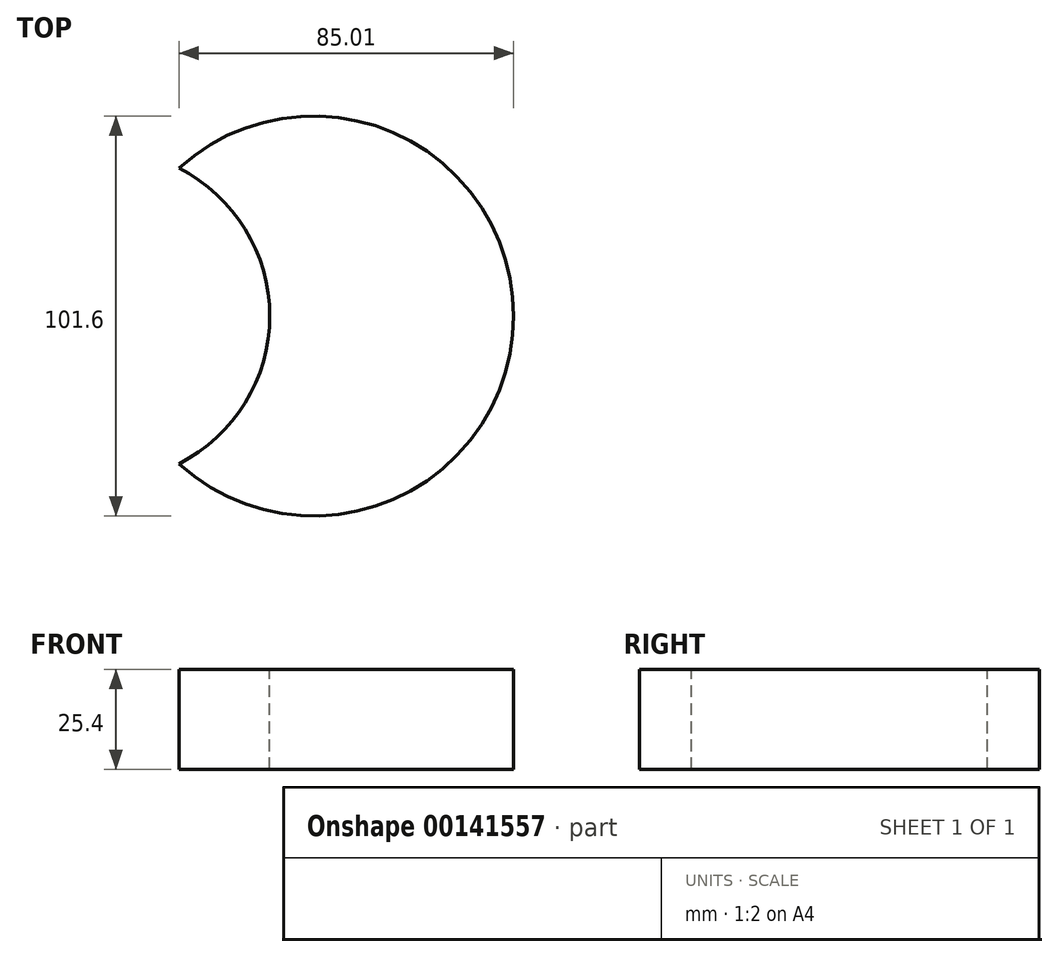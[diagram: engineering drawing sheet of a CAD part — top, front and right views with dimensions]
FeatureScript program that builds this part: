
annotation { "Feature Type Name" : "Feature", "Feature Type Description" : "" }
export const myFeature = defineFeature(function(context is Context, id is Id, definition is map)
    precondition{}
    {
        {
            var Q0;
            Q0=qCreatedBy(makeId("Top.planeOp"),FACE);
            var sketch = newSketch(context, id + "F0", { "sketchPlane" : qUnion([Q0])});
            skCircle(sketch, "E0", {"center": v(0, 0) * mm, "radius": 50.8 * mm});
            skSolve(sketch);
        }
        {
            var Q0;
            Q0=makeQuery(id+"F0.imprint","IMPRINT",FACE,{"disambiguationData":[TD([[makeQuery(id+"F0.imprint","IMPRINT",EDGE,{"derivedFrom":sQuery(id+"F0.wireOp",EDGE,"E0")}),1.0]])]});
            extrude(context, id + "F1", {"entities" : qUnion([Q0]), "depth" : 25.4 * mm});
        }
        {
            var Q0;
            Q0=makeQuery(id+"F1.opExtrude","CAP_FACE",FACE,{"disambiguationData":[OSD([sQuery(id+"F0.wireOp",EDGE,"E0")])],"isStart":false});
            var sketch = newSketch(context, id + "F2", { "sketchPlane" : qUnion([Q0])});
            skCircle(sketch, "E1", {"center": v(-53.22, 0) * mm, "radius": 42.1 * mm});
            skSolve(sketch);
        }
        {
            var Q0;
            {var subQ0=sQuery(id+"F2.wireOp",EDGE,"E1");var subQ1=makeQuery(id+"F1.opExtrude","CAP_EDGE",EDGE,{"disambiguationData":[OSD([sQuery(id+"F0.wireOp",EDGE,"E0")])],"isStart":false});var subQ2=makeQuery(id+"F2.imprint","INTERSECT",VERTEX,{"disambiguationData":[OD(0.0)],"derivedFrom":[subQ1,subQ0]});Q0=makeQuery(id+"F2.imprint","IMPRINT",FACE,{"disambiguationData":[TD([[makeQuery(id+"F2.imprint","IMPRINT",EDGE,{"disambiguationData":[TD([[subQ2,1.0]])],"derivedFrom":subQ0}),1.0]])]});}
            var Q1;
            {var subQ0=sQuery(id+"F2.wireOp",EDGE,"E1");var subQ1=makeQuery(id+"F1.opExtrude","CAP_EDGE",EDGE,{"disambiguationData":[OSD([sQuery(id+"F0.wireOp",EDGE,"E0")])],"isStart":false});var subQ2=makeQuery(id+"F2.imprint","INTERSECT",VERTEX,{"disambiguationData":[OD(0.0)],"derivedFrom":[subQ1,subQ0]});Q1=makeQuery(id+"F2.imprint","IMPRINT",FACE,{"disambiguationData":[TD([[makeQuery(id+"F2.imprint","IMPRINT",EDGE,{"disambiguationData":[TD([[subQ2,-1.0]])],"derivedFrom":subQ0}),1.0]])]});}
            extrude(context, id + "F3", {"entities" : qUnion([Q0, Q1]), "operationType" : NewBodyOperationType.REMOVE, "oppositeDirection" : true, "depth" : 25.4 * mm});
        }
    });
